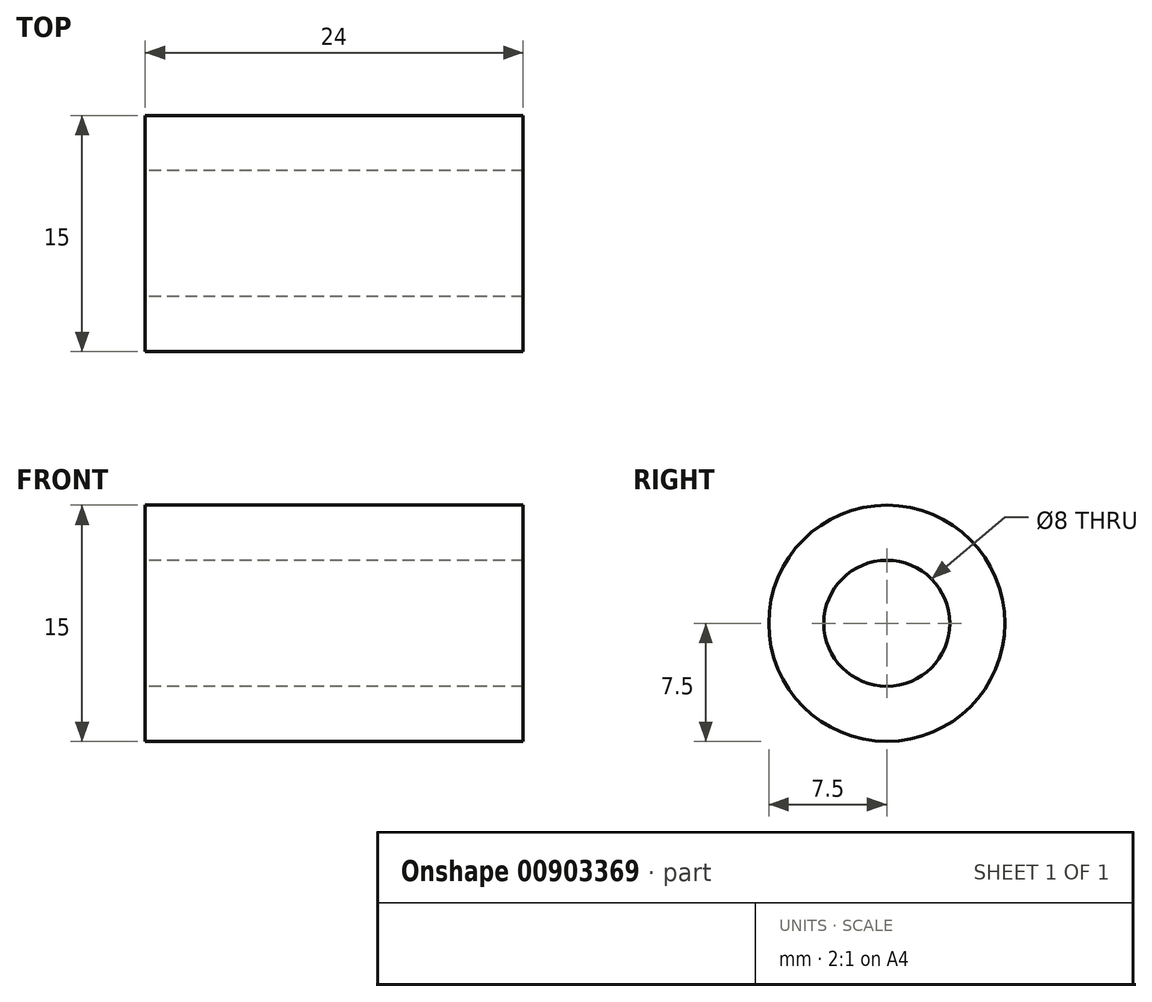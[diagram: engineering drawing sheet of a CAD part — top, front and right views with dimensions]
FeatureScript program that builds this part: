
annotation { "Feature Type Name" : "Feature", "Feature Type Description" : "" }
export const myFeature = defineFeature(function(context is Context, id is Id, definition is map)
    precondition{}
    {
        {
            var Q0;
            Q0=qCreatedBy(makeId("Right.planeOp"),FACE);
            var sketch = newSketch(context, id + "F0", { "sketchPlane" : qUnion([Q0])});
            skCircle(sketch, "E0", {"center": v(0, 0) * mm, "radius": 7.5 * mm});
            skCircle(sketch, "E1", {"center": v(0, 0) * mm, "radius": 4 * mm});
            skSolve(sketch);
        }
        {
            var Q0;
            Q0 = qSketchRegion(id + "F0", true);
            extrude(context, id + "F1", {"entities" : qUnion([Q0]), "endBound" : BoundingType.SYMMETRIC, "depth" : 24 * mm, "offsetDistance" : 25 * mm});
        }
    });
